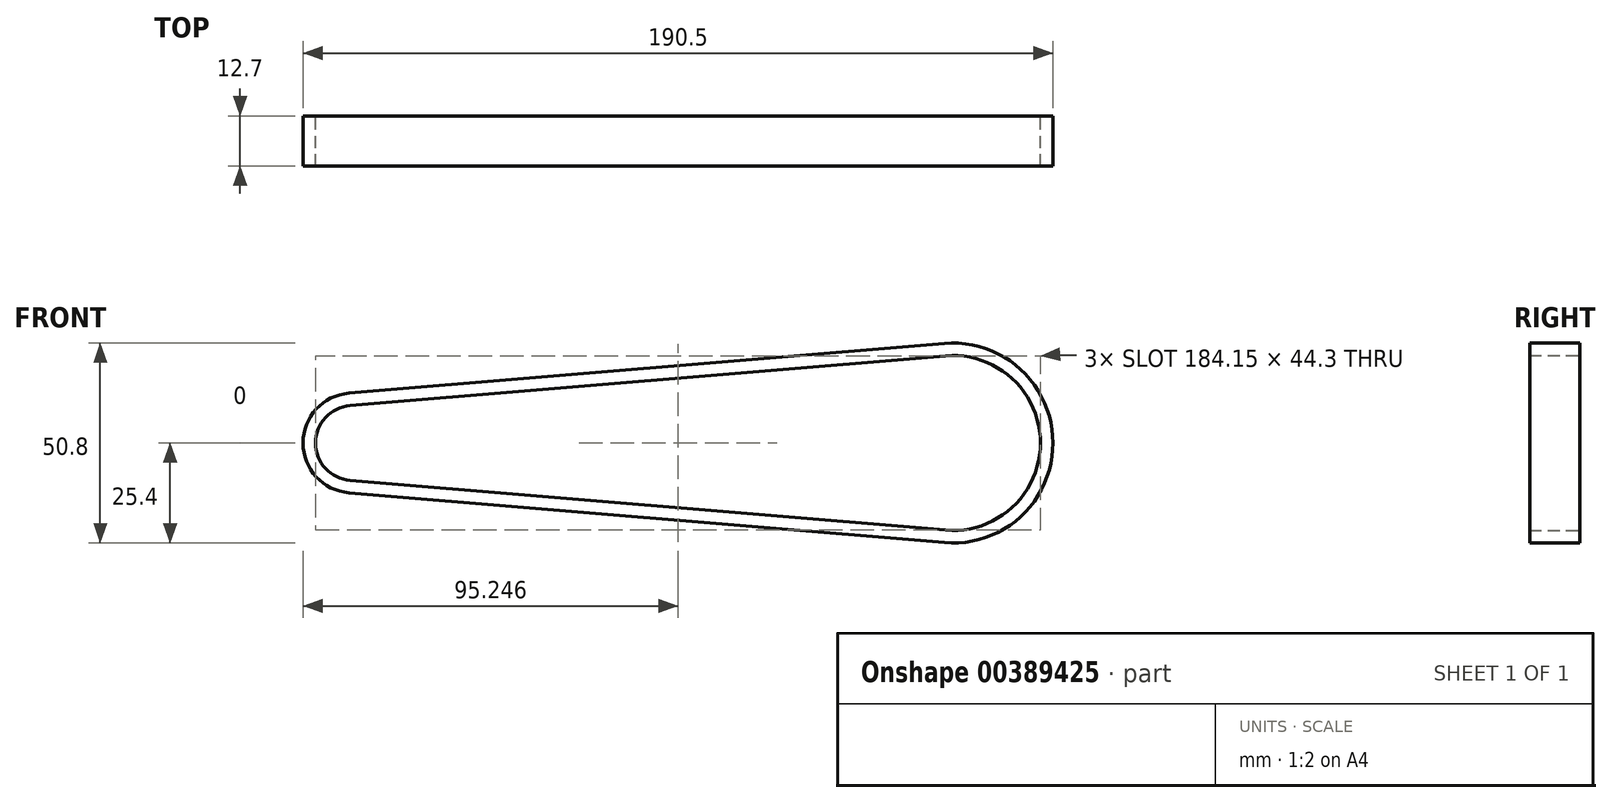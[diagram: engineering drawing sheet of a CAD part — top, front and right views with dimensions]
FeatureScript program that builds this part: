
annotation { "Feature Type Name" : "Feature", "Feature Type Description" : "" }
export const myFeature = defineFeature(function(context is Context, id is Id, definition is map)
    precondition{}
    {
        {
            var Q0;
            Q0=qCreatedBy(makeId("Front.planeOp"),FACE);
            var sketch = newSketch(context, id + "F0", { "sketchPlane" : qUnion([Q0])});
            skArc(sketch, "E0", {"start": v(-31.37, 9.5) * mm, "mid": v(-40.1, 0) * mm, "end": v(-31.37, -9.5) * mm});
            skArc(sketch, "E1", {"start": v(119.97, -22.15) * mm, "mid": v(144.05, 0) * mm, "end": v(119.97, 22.15) * mm});
            skLineSegment(sketch, "E2", {"start": v(-31.37, 9.5) * mm, "end": v(119.97, 22.15) * mm});
            skLineSegment(sketch, "E3", {"start": v(-31.37, -9.5) * mm, "end": v(119.97, -22.15) * mm});
            skArc(sketch, "E4", {"start": v(-31.63, 12.66) * mm, "mid": v(-43.27, 0) * mm, "end": v(-31.63, -12.66) * mm});
            skArc(sketch, "E5", {"start": v(119.7, -25.31) * mm, "mid": v(147.23, 0) * mm, "end": v(119.7, 25.31) * mm});
            skLineSegment(sketch, "E6", {"start": v(-31.63, 12.66) * mm, "end": v(119.7, 25.31) * mm});
            skLineSegment(sketch, "E7", {"start": v(-31.63, -12.66) * mm, "end": v(119.7, -25.31) * mm});
            skPoint(sketch, "E8.end.orphan", {"position": v(-71.67, 0) * mm});
            skPoint(sketch, "E8.start.orphan", {"position": v(-82.72, 0) * mm});
            skSolve(sketch);
        }
        {
            var Q0;
            Q0 = qSketchRegion(id + "F0", true);
            extrude(context, id + "F1", {"entities" : qUnion([Q0]), "depth" : 12.7 * mm});
        }
    });
